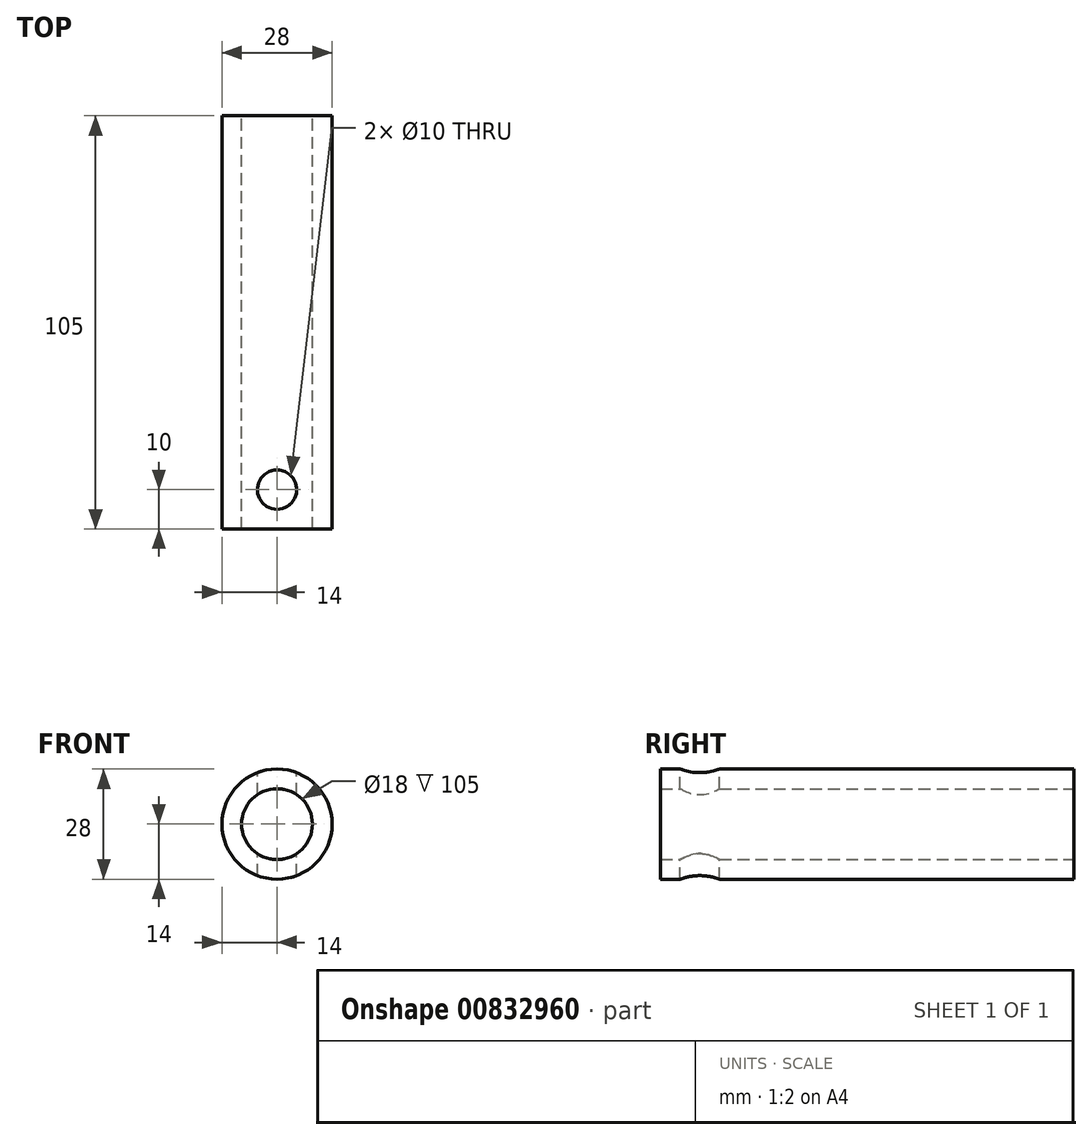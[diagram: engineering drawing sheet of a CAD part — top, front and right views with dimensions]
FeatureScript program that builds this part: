
annotation { "Feature Type Name" : "Feature", "Feature Type Description" : "" }
export const myFeature = defineFeature(function(context is Context, id is Id, definition is map)
    precondition{}
    {
        {
            var Q0;
            Q0=qCreatedBy(makeId("Front.planeOp"),FACE);
            var sketch = newSketch(context, id + "F0", { "sketchPlane" : qUnion([Q0])});
            skCircle(sketch, "E0", {"center": v(0, 0) * mm, "radius": 9 * mm});
            skCircle(sketch, "E1", {"center": v(0, 0) * mm, "radius": 14 * mm});
            skSolve(sketch);
        }
        {
            var Q0;
            Q0=makeQuery(id+"F0.imprint","IMPRINT",FACE,{"disambiguationData":[TD([[makeQuery(id+"F0.imprint","IMPRINT",EDGE,{"derivedFrom":sQuery(id+"F0.wireOp",EDGE,"E0")}),-1.0]])]});
            extrude(context, id + "F1", {"entities" : qUnion([Q0]), "depth" : 105 * mm, "offsetDistance" : 25 * mm});
        }
        {
            var Q0;
            Q0=qCreatedBy(makeId("Top.planeOp"),FACE);
            var sketch = newSketch(context, id + "F2", { "sketchPlane" : qUnion([Q0])});
            skLineSegment(sketch, "E2", {"start": v(0, 0) * mm, "end": v(0, -95) * mm, "construction": true});
            skCircle(sketch, "E3", {"center": v(0, -95) * mm, "radius": 5 * mm});
            skSolve(sketch);
        }
        {
            var Q0;
            Q0=makeQuery(id+"F2.imprint","IMPRINT",FACE,{"disambiguationData":[TD([[makeQuery(id+"F2.imprint","IMPRINT",EDGE,{"derivedFrom":sQuery(id+"F2.wireOp",EDGE,"E3")}),1.0]])]});
            extrude(context, id + "F3", {"entities" : qUnion([Q0]), "operationType" : NewBodyOperationType.REMOVE, "oppositeDirection" : true, "depth" : 67.2 * mm, "offsetDistance" : 25 * mm, "symmetric" : true});
        }
    });
